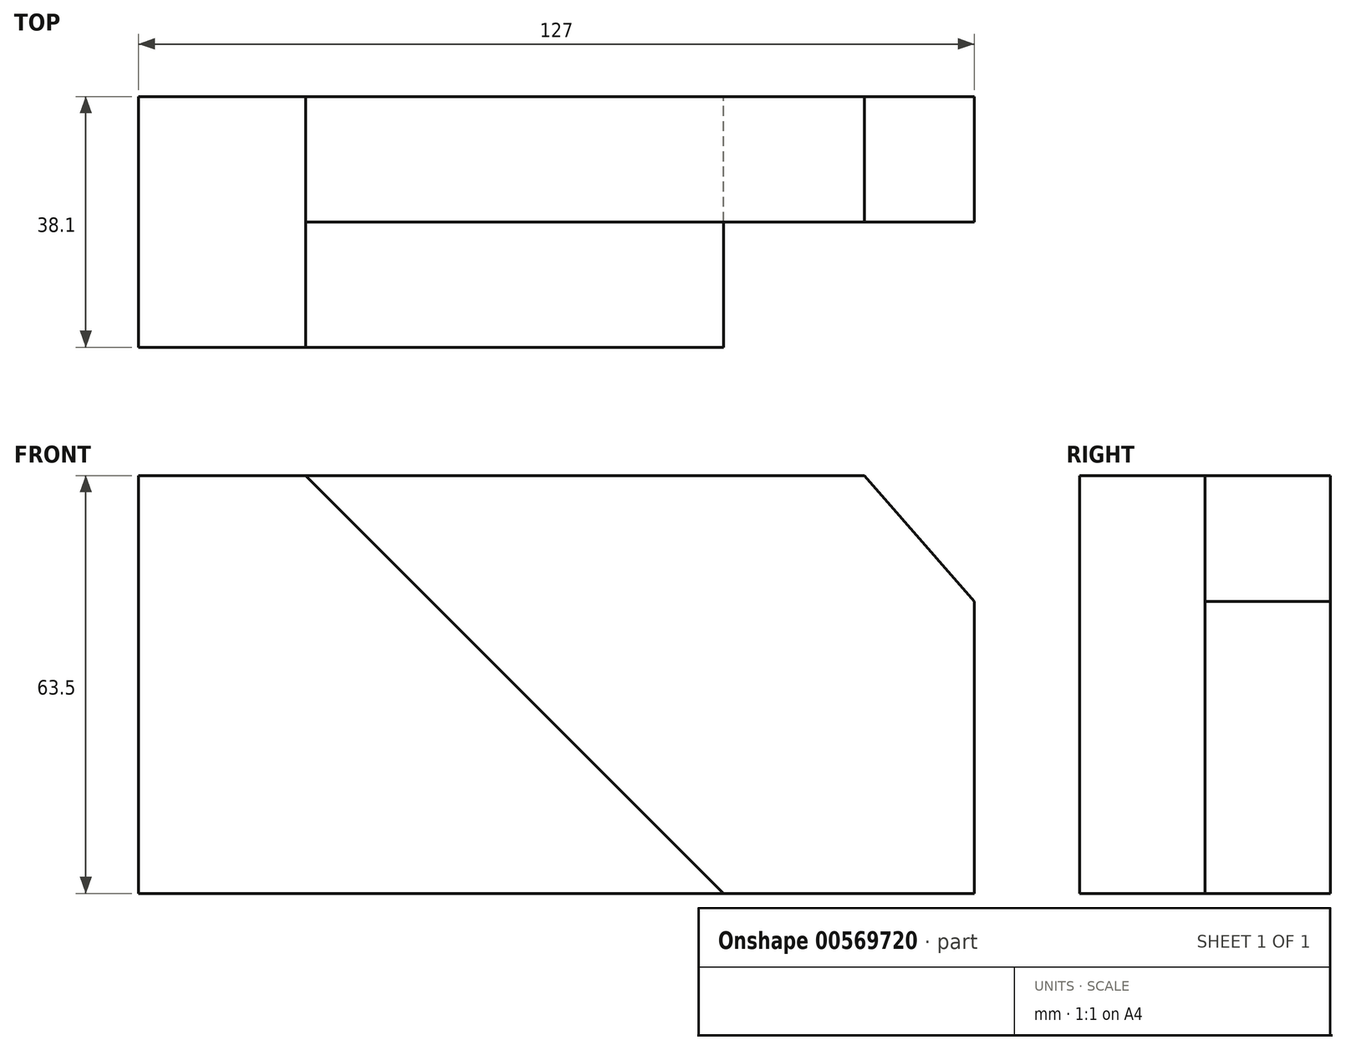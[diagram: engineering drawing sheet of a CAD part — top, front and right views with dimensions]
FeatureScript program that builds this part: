
annotation { "Feature Type Name" : "Feature", "Feature Type Description" : "" }
export const myFeature = defineFeature(function(context is Context, id is Id, definition is map)
    precondition{}
    {
        {
            var Q0;
            Q0=qCreatedBy(makeId("Front.planeOp"),FACE);
            var sketch = newSketch(context, id + "F0", { "sketchPlane" : qUnion([Q0])});
            skLineSegment(sketch, "E0", {"start": v(-70.03, 43.47) * mm, "end": v(-70.03, -20.03) * mm});
            skLineSegment(sketch, "E1", {"start": v(-70.03, -20.03) * mm, "end": v(56.97, -20.03) * mm});
            skLineSegment(sketch, "E2", {"start": v(56.97, -20.03) * mm, "end": v(56.97, 43.47) * mm});
            skLineSegment(sketch, "E3", {"start": v(56.97, 43.47) * mm, "end": v(-70.03, 43.47) * mm});
            skLineSegment(sketch, "E4", {"start": v(56.97, 24.35) * mm, "end": v(40.24, 43.47) * mm});
            skLineSegment(sketch, "E5", {"start": v(-44.63, 43.47) * mm, "end": v(18.87, -20.03) * mm});
            skSolve(sketch);
        }
        {
            var Q0;
            {var subQ0=sQuery(id+"F0.wireOp",EDGE,"E0");Q0=makeQuery(id+"F0.imprint","IMPRINT",FACE,{"disambiguationData":[TD([[makeQuery(id+"F0.imprint","IMPRINT",EDGE,{"derivedFrom":subQ0}),1.0]])]});}
            extrude(context, id + "F1", {"entities" : qUnion([Q0]), "depth" : 38.1 * mm, "offsetDistance" : 25.4 * mm});
        }
        {
            var Q0;
            {var subQ0=sQuery(id+"F0.wireOp",EDGE,"E4");Q0=makeQuery(id+"F0.imprint","IMPRINT",FACE,{"disambiguationData":[TD([[makeQuery(id+"F0.imprint","IMPRINT",EDGE,{"derivedFrom":subQ0}),1.0]])]});}
            extrude(context, id + "F2", {"entities" : qUnion([Q0]), "depth" : 19.05 * mm, "offsetDistance" : 25.4 * mm});
        }
    });
